# Revit family: 401806 HYDROFLEX TOP 1000
name_source: partatom
category: Apparecchi per illuminazione
units: mm (PartAtom-declared; Revit-internal decimal feet)

## family parameters
Basato su piano di lavoro = No
Condiviso = Sì
Mantieni orientamento annotazione = No
Punto di calcolo locali = No
Quota connettore circolare = Usa diametro
Sempre verticale = Sì
Sorgente d'illuminazione = Sì
Taglio con vuoti quando caricato = No
Tipo di parte = Normale

## types (1)
- ALLOY
    Angolo inclinazione = 0.00°
    Available Optics = DIFFUSED
    Files diagrammi fotometrici = https://puk.it
    Filtro dei colori = 16777215
    Finish color = Materiale __RGBA_1.000_1.000_1.000_1.000
    IP Rating = IP68
    Ligjt Source = LED
    Material = high performances Polyurethane, UV resistant, saltwater resistant
    Modello = HYDROFLEX TOP 1000
    Produttore = PUK
    Prospetto di default = 2023 mm
    URL = https://puk.it
    Variazione temperatura colore lampada con luminosità attenuata = <Nessuno>
    Voltage = 24V DC
    Wattage = 10W x METER
